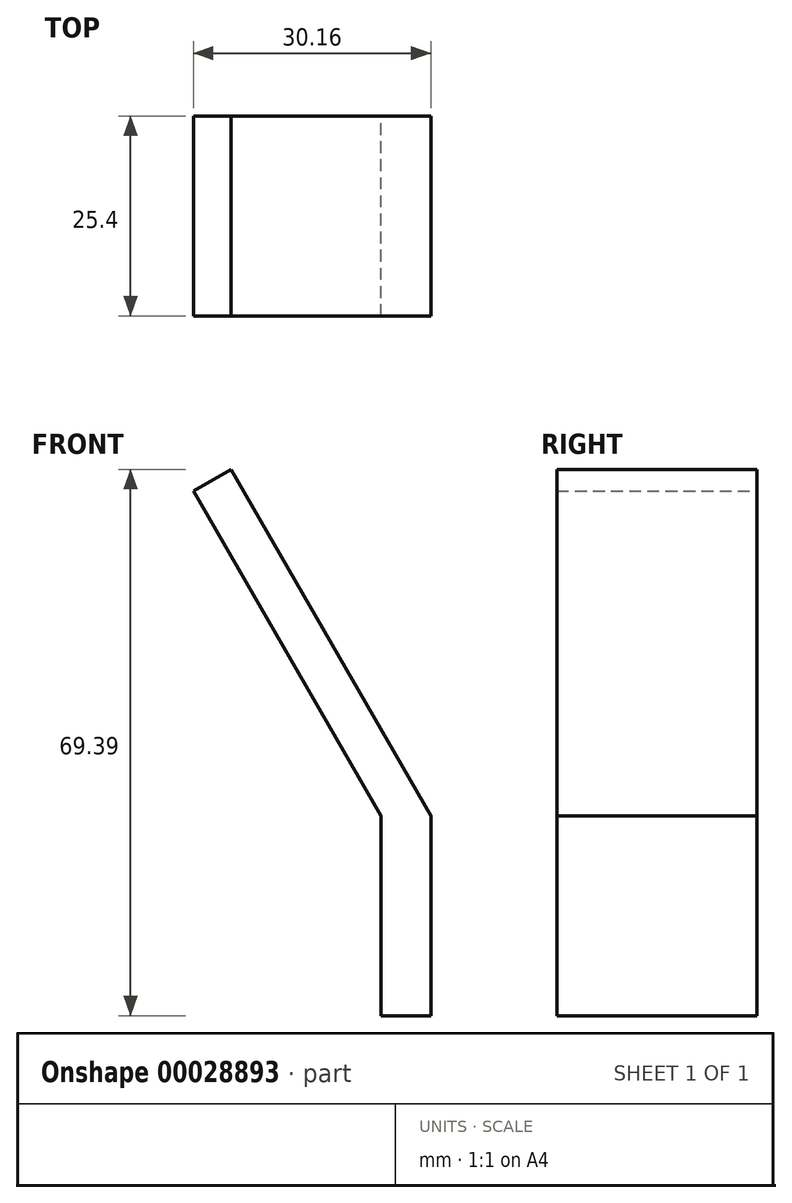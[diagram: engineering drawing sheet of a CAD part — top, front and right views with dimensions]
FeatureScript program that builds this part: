
annotation { "Feature Type Name" : "Feature", "Feature Type Description" : "" }
export const myFeature = defineFeature(function(context is Context, id is Id, definition is map)
    precondition{}
    {
        {
            var Q0;
            Q0=qCreatedBy(makeId("Front.planeOp"),FACE);
            var sketch = newSketch(context, id + "F0", { "sketchPlane" : qUnion([Q0])});
            skLineSegment(sketch, "E0.bottom", {"start": v(1.6, 7.35) * mm, "end": v(7.95, 7.35) * mm});
            skLineSegment(sketch, "E0.top", {"start": v(1.6, -18.05) * mm, "end": v(7.95, -18.05) * mm});
            skLineSegment(sketch, "E0.left", {"start": v(1.6, 7.35) * mm, "end": v(1.6, -18.05) * mm});
            skLineSegment(sketch, "E0.right", {"start": v(7.95, 7.35) * mm, "end": v(7.95, -18.05) * mm});
            skLineSegment(sketch, "E1", {"start": v(7.95, 7.35) * mm, "end": v(-17.45, 51.34) * mm});
            skLineSegment(sketch, "E2", {"start": v(-17.45, 51.34) * mm, "end": v(-22.21, 48.6) * mm});
            skLineSegment(sketch, "E3", {"start": v(-22.21, 48.6) * mm, "end": v(1.6, 7.35) * mm});
            skSolve(sketch);
        }
        {
            var Q0;
            Q0=makeQuery(id+"F0.imprint","IMPRINT",FACE,{"disambiguationData":[TD([[makeQuery(id+"F0.imprint","IMPRINT",EDGE,{"derivedFrom":sQuery(id+"F0.wireOp",EDGE,"E0.bottom")}),1.0]])]});
            var Q1;
            Q1=makeQuery(id+"F0.imprint","IMPRINT",FACE,{"disambiguationData":[TD([[makeQuery(id+"F0.imprint","IMPRINT",EDGE,{"derivedFrom":sQuery(id+"F0.wireOp",EDGE,"E0.bottom")}),-1.0]])]});
            var Q2;
            Q2=sQuery(id+"F0.wireOp",EDGE,"E1");
            var Q3;
            Q3=sQuery(id+"F0.wireOp",EDGE,"E0.right");
            extrude(context, id + "F1", {"entities" : qUnion([Q0, Q1]), "surfaceEntities" : qUnion([Q2, Q3]), "depth" : 25.4 * mm});
        }
    });
